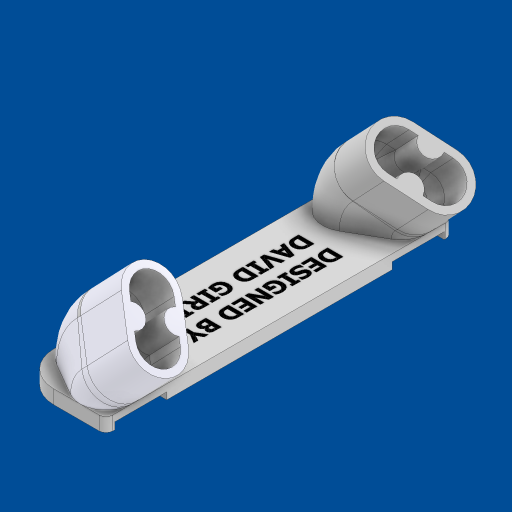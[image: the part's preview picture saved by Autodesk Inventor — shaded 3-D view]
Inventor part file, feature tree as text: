
AUTODESK INVENTOR PART (.ipt)
format: ipt  version: 2023 (Build 270158000, 158)  size: 1,025,536 bytes
history: native  units: mm
features: extrude x17, sketch x12, plane x2, revolve x2, chamfer x2, fillet x2, sweep x1, mirror x1
ambient origin geometry x8: Origin, YZ Plane, XZ Plane, XY Plane, X Axis, Y Axis, Z Axis, Center Point
bodies: Solid1 (feature_tree)
feature tree (39):
  sketch  "Sketch1"  dims[d0=100.0mm d1=25.0mm d2=7.5mm d3=7.5mm d4=60.0deg d5=15.0mm d6=11.0mm d7=11.0mm d8=15.0mm d11=135.0deg]
  plane  "Work Plane1"
  sweep  "Sweep1"
  extrude  "Extrusion1"  Depth=4.0mm TaperAngle=0.0deg
  revolve  "Revolution1"  Angle=45.0deg
  sketch  "Sketch6"  dims[d31=10.0mm d32=45.0deg]
  extrude  "Extrusion4"  TaperAngle=45.0deg  [1 undecoded]
  extrude  "Extrusion5"  Depth=10.0mm
  sketch  "Sketch7"  dims[d33=10.0mm d34=10.0mm]
  extrude  "Extrusion6"  Depth=10.0mm
  extrude  "Extrusion7"  Depth=15.0mm
  mirror  "Mirror4"
  plane  "Work Plane9"
  extrude  "Extrusion8"  Depth=5.5mm
  revolve  "Revolution2"  [1 undecoded]
  extrude  "Extrusion9"  Depth=6.5mm
  sketch  "Sketch19"  dims[d60=5.5mm d61=5.5mm]
  extrude  "Extrusion10"  Depth=15.0mm TaperAngle=0.0deg
  extrude  "Extrusion11"  Depth=10.0mm
  extrude  "Extrusion12"  TaperAngle=90.0deg  [1 undecoded]
  sketch  "Sketch21"  dims[d65=2.0mm d66=6.5mm]
  extrude  "Extrusion13"  Depth=10.0mm
  chamfer  "Chamfer3"  Distance=5.5mm
  extrude  "Extrusion15"  Depth=10.0mm
  extrude  "Extrusion18"  Depth=10.0mm
  fillet  "Fillet2"  Radius=11.0mm
  fillet  "Fillet3"  Radius=11.0mm
  extrude  "Extrusion19"  Depth=10.0mm
  extrude  "Extrusion20"  Depth=10.0mm
  extrude  "Extrusion21"  Depth=10.0mm
  extrude  "Extrusion22"  Depth=10.0mm TaperAngle=0.0deg
  chamfer  "Chamfer6"  Distance=10.0mm
  sketch  "Sketch3"  dims[d12=0.0mm d13=0.0mm d14=4.0mm d15=0.0mm]
  sketch  "Sketch5"  dims[d29=11.389087mm d30=45.0deg]
  sketch  "Sketch14"  dims[d35=45.0deg d37=10.0mm]
  sketch  "Sketch15"  dims[d38=0.977384mm d57=15.0mm]
  sketch  "Sketch20"  dims[d63=11.0mm d64=11.0mm]
  sketch  "Sketch22"  dims[d67=6.5mm d68=15.0mm d69=0.0mm]
  sketch  "Sketch23"  dims[d70=325.0mm d71=0.0mm d72=7.5mm d73=90.0deg d74=7.5mm d75=5.5mm d76=5.5mm d77=15.0mm d78=11.0mm d79=11.0mm d80=2.0mm d81=6.5mm d82=6.5mm d83=10.0mm d84=0.0mm d93=10.0mm d94=0.0mm d115=20.0mm d116=0.0mm d131=8.726646mm d132=300.0mm d133=0.0mm d134=15.0mm d135=300.0mm d136=0.0mm d137=11.0mm d138=11.0mm d139=2.0mm d140=6.5mm d141=6.5mm d142=10.0mm d143=0.0mm d144=40.0mm d145=0.0mm d146=25.0mm d147=100.0mm d150=15.0mm d151=5.5mm d152=2.0mm d153=0.0mm d156=2.0mm d157=4.0mm d158=45.0deg d162=549.891mm d163=50.0mm d164=100.0mm d167=2.5mm d169=15.0mm d170=17.5mm d171=17.5mm d174=10.0mm d175=300.0mm d176=0.0mm d177=7.5mm d183=2.0mm d184=0.0mm d185=2.0mm d186=10.0mm d187=3.0mm d188=0.0mm d189=15.0mm d190=0.0mm d191=1.0mm d192=0.0mm d193=6.5mm d194=5.0mm d195=0.0mm d199=2.0mm d200=4.0mm d201=45.0deg d178=0.872665mm d196=0.5mm d197=0.872665mm]
note: 3 required parameter values undecoded (feature->parameter linkage not recoverable at this tier; creation-order binding heuristic only, values carry confidence <= 0.55)